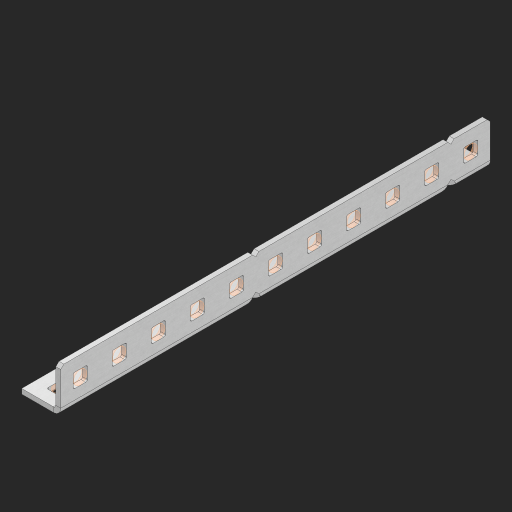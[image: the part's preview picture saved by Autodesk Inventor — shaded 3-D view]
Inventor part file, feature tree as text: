
AUTODESK INVENTOR PART (.ipt)
format: ipt  version: 2023 (Build 270158000, 158)  size: 526,336 bytes
history: native  units: in
note: dims shown in document units (in); Inventor stores cm internally (conversion verified against a paired STEP export)
features: other x27, extrude x21, sheet_metal_op x10, sketch x8, mirror x1, pattern_linear x1, chamfer x1
ambient origin geometry x8: Origin, YZ Plane, XZ Plane, XY Plane, X Axis, Y Axis, Z Axis, Center Point
bodies: Solid1 (feature_tree), Body (feature_tree)
feature tree (69):
  other  "Flange Pattern Plane"
  sheet_metal_op  "Flange Pattern"
  sheet_metal_op  "Body Pattern"
  other  "Arc Length"
  mirror  "Notch Mirror"
  pattern_linear  "Notch Pattern"  Spacing1=0.25in  [1 undecoded]
  chamfer  "End Chamfer"
  extrude  "Half Cut"  Depth=0.0625in
  sketch  "Sketch1"  dims[d0=1.5in]
  other  "Plate1"
  sketch  "Sketch2"  dims[d1=5.5in]
  other  "Plate2"
  sheet_metal_op  "Bend1"
  sheet_metal_op  "Corner1"
  sketch  "Sketch3"  dims[d2=0.0625in]
  other  "Flange Pattern Sketch"
  sketch  "Sketch7"  dims[d3=0.0625in]
  other  "Srf1"
  other  "Srf2"
  sketch  "Sketch8"  dims[d4=0.0312in]
  sketch  "Sketch9"  dims[d5=0.125in]
  other  "Srf91"
  sheet_metal_op  "Body Pattern Sketch"
  other  "Srf92"
  sketch  "Sketch13"  dims[d6=0.0625in]
  sketch  "Sketch14"  dims[d7=0.5in d8=90.0deg d9=0.0312in d10=0.25in d11=0.0625in d12=0.0625in d16=0.182in d17=0.02in d18=0.0625in d19=0.0in d20=0.25in d21=0.25in d46=0.172in d47=1.0in d48=0.0in d49=0.182in d50=0.02in d51=0.25in d52=0.25in d53=0.0625in d54=0.0in d55=0.172in d56=1.0in d57=0.0in d60=4.3307in d62=0.5in d63=0.3937in d65=0.5in d85=0.1473in d86=0.1782in d88=0.04in d89=0.0625in d90=0.0in d91=0.04in d92=0.0491in d95=2.5in d96=0.04in d97=0.25in d98=45.0deg d101=0.0in d102=2.497in d131=0.5in d132=4.3307in d134=0.5in d139=0.5in]
  other  "Srf856"
  other  "Srf1310"
  other  "Srf1311"
  other  "Srf1312"
  other  "Srf1376"
  other  "Srf1377"
  other  "Srf1728"
  other  "Srf1755"
  other  "Srf1878"
  other  "Srf1879"
  other  "Srf1880"
  other  "Srf1881"
  other  "Srf1882"
  other  "Srf1942"
  other  "Srf1943"
  other  "Srf1944"
  other  "Srf1945"
  other  "Srf1946"
  sheet_metal_op  "Flange Stamp"
  sheet_metal_op  "Flange Circle"
  sheet_metal_op  "Body Stamp"
  sheet_metal_op  "Body Circle"
  sheet_metal_op  "Notch"
  extrude  "ExtrusionSrf2"  Depth=0.0625in
  extrude  "ExtrusionSrf92"  Depth=0.5in
  extrude  "ExtrusionSrf856"  Depth=0.02in
  extrude  "ExtrusionSrf1310"  Depth=0.0625in
  extrude  "ExtrusionSrf1311"  TaperAngle=0.0deg  [1 undecoded]
  extrude  "ExtrusionSrf1312"  Depth=0.5in
  extrude  "ExtrusionSrf1376"  Depth=0.5in
  extrude  "ExtrusionSrf1377"  Depth=0.5in
  extrude  "ExtrusionSrf1728"  Depth=0.5in TaperAngle=0.0deg
  extrude  "ExtrusionSrf1755"  Depth=0.5in
  extrude  "ExtrusionSrf1878"  Depth=0.02in
  extrude  "ExtrusionSrf1879"  Depth=0.5in
  extrude  "ExtrusionSrf1880"  Depth=0.5in
  extrude  "ExtrusionSrf1881"  Depth=0.0625in
  extrude  "ExtrusionSrf1882"  TaperAngle=0.0deg  [1 undecoded]
  extrude  "ExtrusionSrf1942"  Depth=0.5in
  extrude  "ExtrusionSrf1943"  Depth=0.5in TaperAngle=0.0deg
  extrude  "ExtrusionSrf1944"  Depth=0.5in
  extrude  "ExtrusionSrf1945"  Depth=0.5in
  extrude  "ExtrusionSrf1946"  Depth=0.5in
note: 3 required parameter values undecoded (feature->parameter linkage not recoverable at this tier; creation-order binding heuristic only, values carry confidence <= 0.55)
